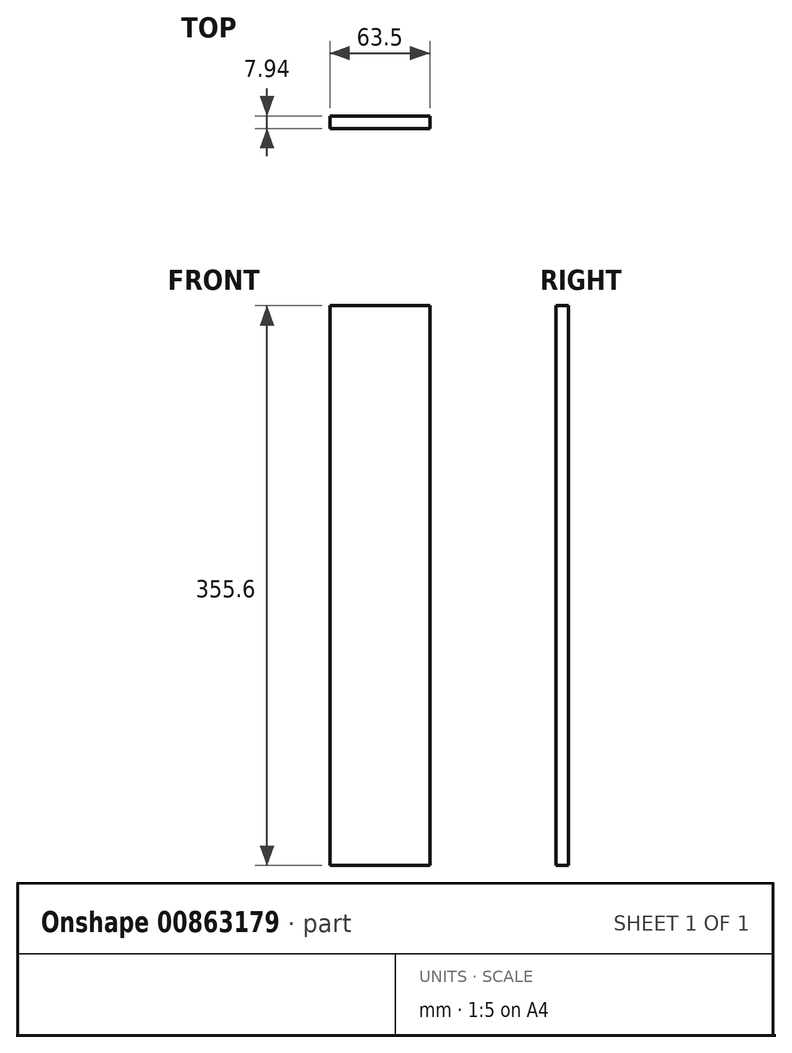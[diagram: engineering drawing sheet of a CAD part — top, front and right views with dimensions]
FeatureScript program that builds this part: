
annotation { "Feature Type Name" : "Feature", "Feature Type Description" : "" }
export const myFeature = defineFeature(function(context is Context, id is Id, definition is map)
    precondition{}
    {
        {
            var Q0;
            Q0=qCreatedBy(makeId("Front.planeOp"),FACE);
            var sketch = newSketch(context, id + "F0", { "sketchPlane" : qUnion([Q0])});
            skLineSegment(sketch, "E0.bottom", {"start": v(31.75, 177.8) * mm, "end": v(-31.75, 177.8) * mm});
            skLineSegment(sketch, "E0.top", {"start": v(31.75, -177.8) * mm, "end": v(-31.75, -177.8) * mm});
            skLineSegment(sketch, "E0.left", {"start": v(31.75, 177.8) * mm, "end": v(31.75, -177.8) * mm});
            skLineSegment(sketch, "E0.right", {"start": v(-31.75, 177.8) * mm, "end": v(-31.75, -177.8) * mm});
            skPoint(sketch, "E0.middle", {"position": v(0, 0) * mm});
            skSolve(sketch);
        }
        {
            var Q0;
            Q0=makeQuery(id+"F0.imprint","IMPRINT",FACE,{"disambiguationData":[TD([[makeQuery(id+"F0.imprint","IMPRINT",EDGE,{"derivedFrom":sQuery(id+"F0.wireOp",EDGE,"E0.bottom")}),1.0]])]});
            extrude(context, id + "F1", {"entities" : qUnion([Q0]), "depth" : 7.94 * mm, "offsetDistance" : 25.4 * mm});
        }
    });
